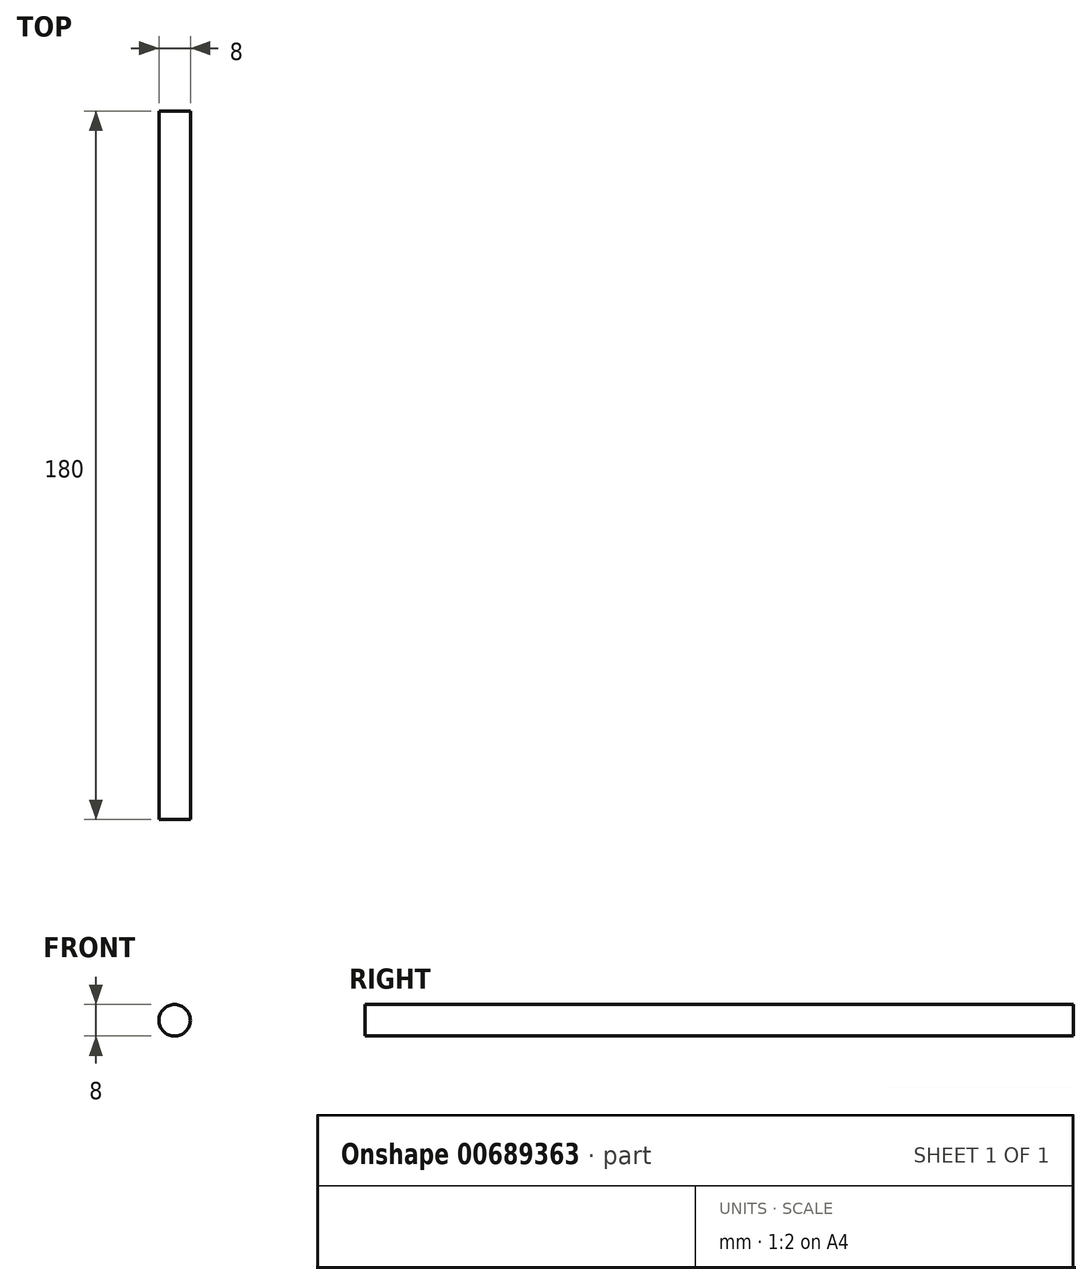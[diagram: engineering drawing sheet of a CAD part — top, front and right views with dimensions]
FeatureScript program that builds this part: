
annotation { "Feature Type Name" : "Feature", "Feature Type Description" : "" }
export const myFeature = defineFeature(function(context is Context, id is Id, definition is map)
    precondition{}
    {
        {
            var Q0;
            Q0=qCreatedBy(makeId("Front.planeOp"),FACE);
            var sketch = newSketch(context, id + "F0", { "sketchPlane" : qUnion([Q0])});
            skCircle(sketch, "E0", {"center": v(0, 0) * mm, "radius": 4 * mm});
            skSolve(sketch);
        }
        {
            var Q0;
            Q0=qSketchRegion(id+"F0",true);
            extrude(context, id + "F1", {"entities" : qUnion([Q0]), "depth" : 180 * mm});
        }
    });
